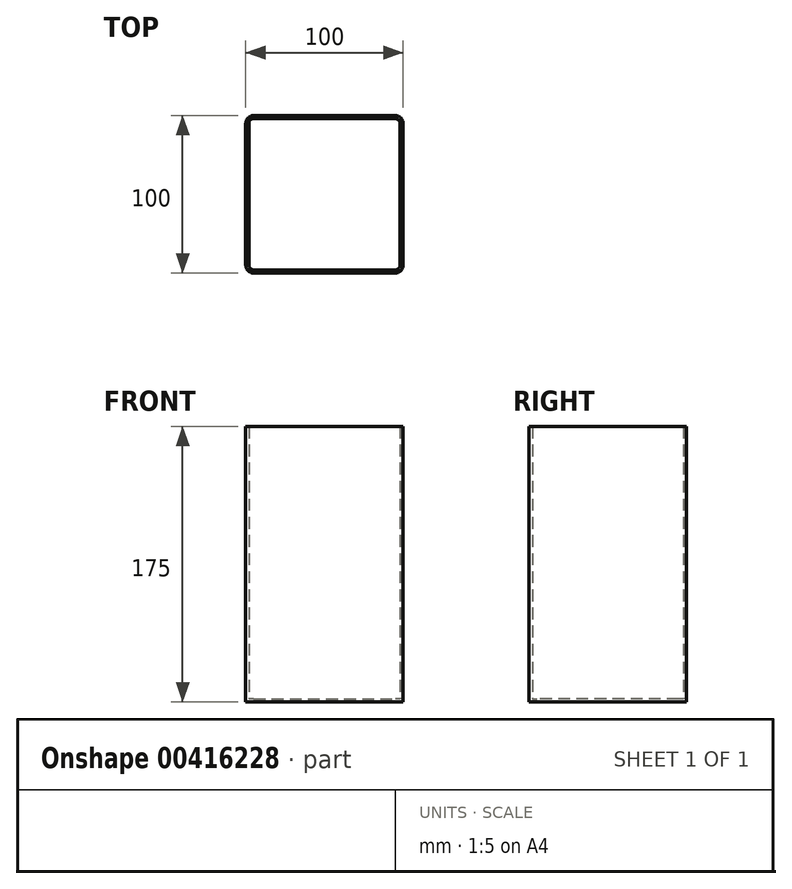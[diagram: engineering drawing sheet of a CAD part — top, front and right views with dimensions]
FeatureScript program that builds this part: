
annotation { "Feature Type Name" : "Feature", "Feature Type Description" : "" }
export const myFeature = defineFeature(function(context is Context, id is Id, definition is map)
    precondition{}
    {
        {
            var Q0;
            Q0=qCreatedBy(makeId("Top.planeOp"),FACE);
            var sketch = newSketch(context, id + "F0", { "sketchPlane" : qUnion([Q0])});
            skLineSegment(sketch, "E0.bottom", {"start": v(-45, 50) * mm, "end": v(45, 50) * mm});
            skLineSegment(sketch, "E0.top", {"start": v(-45, -50) * mm, "end": v(45, -50) * mm});
            skLineSegment(sketch, "E0.left", {"start": v(-50, 45) * mm, "end": v(-50, -45) * mm});
            skLineSegment(sketch, "E0.right", {"start": v(50, 45) * mm, "end": v(50, -45) * mm});
            skPoint(sketch, "E0.middle", {"position": v(0, 0) * mm});
            skPoint(sketch, "E1.visualSharp", {"position": v(-50, 50) * mm});
            skArc(sketch, "E1.filletArc", {"start": v(-45, 50) * mm, "mid": v(-48.54, 48.54) * mm, "end": v(-50, 45) * mm});
            skPoint(sketch, "E2.visualSharp", {"position": v(50, 50) * mm});
            skArc(sketch, "E2.filletArc", {"start": v(50, 45) * mm, "mid": v(48.54, 48.54) * mm, "end": v(45, 50) * mm});
            skPoint(sketch, "E3.visualSharp", {"position": v(50, -50) * mm});
            skArc(sketch, "E3.filletArc", {"start": v(45, -50) * mm, "mid": v(48.54, -48.54) * mm, "end": v(50, -45) * mm});
            skPoint(sketch, "E4.visualSharp", {"position": v(-50, -50) * mm});
            skArc(sketch, "E4.filletArc", {"start": v(-50, -45) * mm, "mid": v(-48.54, -48.54) * mm, "end": v(-45, -50) * mm});
            skArc(sketch, "E5.0", {"start": v(-45, 48) * mm, "mid": v(-47.12, 47.12) * mm, "end": v(-48, 45) * mm});
            skLineSegment(sketch, "E5.1", {"start": v(-45, 48) * mm, "end": v(45, 48) * mm});
            skLineSegment(sketch, "E5.2", {"start": v(-48, 45) * mm, "end": v(-48, -45) * mm});
            skArc(sketch, "E5.3", {"start": v(48, 45) * mm, "mid": v(47.12, 47.12) * mm, "end": v(45, 48) * mm});
            skArc(sketch, "E5.4", {"start": v(-48, -45) * mm, "mid": v(-47.12, -47.12) * mm, "end": v(-45, -48) * mm});
            skLineSegment(sketch, "E5.5", {"start": v(-45, -48) * mm, "end": v(45, -48) * mm});
            skArc(sketch, "E5.6", {"start": v(45, -48) * mm, "mid": v(47.12, -47.12) * mm, "end": v(48, -45) * mm});
            skLineSegment(sketch, "E5.7", {"start": v(48, 45) * mm, "end": v(48, -45) * mm});
            skSolve(sketch);
        }
        {
            var Q0;
            Q0=makeQuery(id+"F0.imprint","IMPRINT",FACE,{"disambiguationData":[TD([[makeQuery(id+"F0.imprint","IMPRINT",EDGE,{"derivedFrom":sQuery(id+"F0.wireOp",EDGE,"E5.0")}),1.0]])]});
            extrude(context, id + "F1", {"entities" : qUnion([Q0]), "depth" : 2 * mm});
        }
        {
            var Q0;
            Q0=makeQuery(id+"F0.imprint","IMPRINT",FACE,{"disambiguationData":[TD([[makeQuery(id+"F0.imprint","IMPRINT",EDGE,{"derivedFrom":sQuery(id+"F0.wireOp",EDGE,"E0.bottom")}),-1.0]])]});
            extrude(context, id + "F2", {"entities" : qUnion([Q0]), "operationType" : NewBodyOperationType.ADD, "depth" : 175 * mm});
        }
    });
